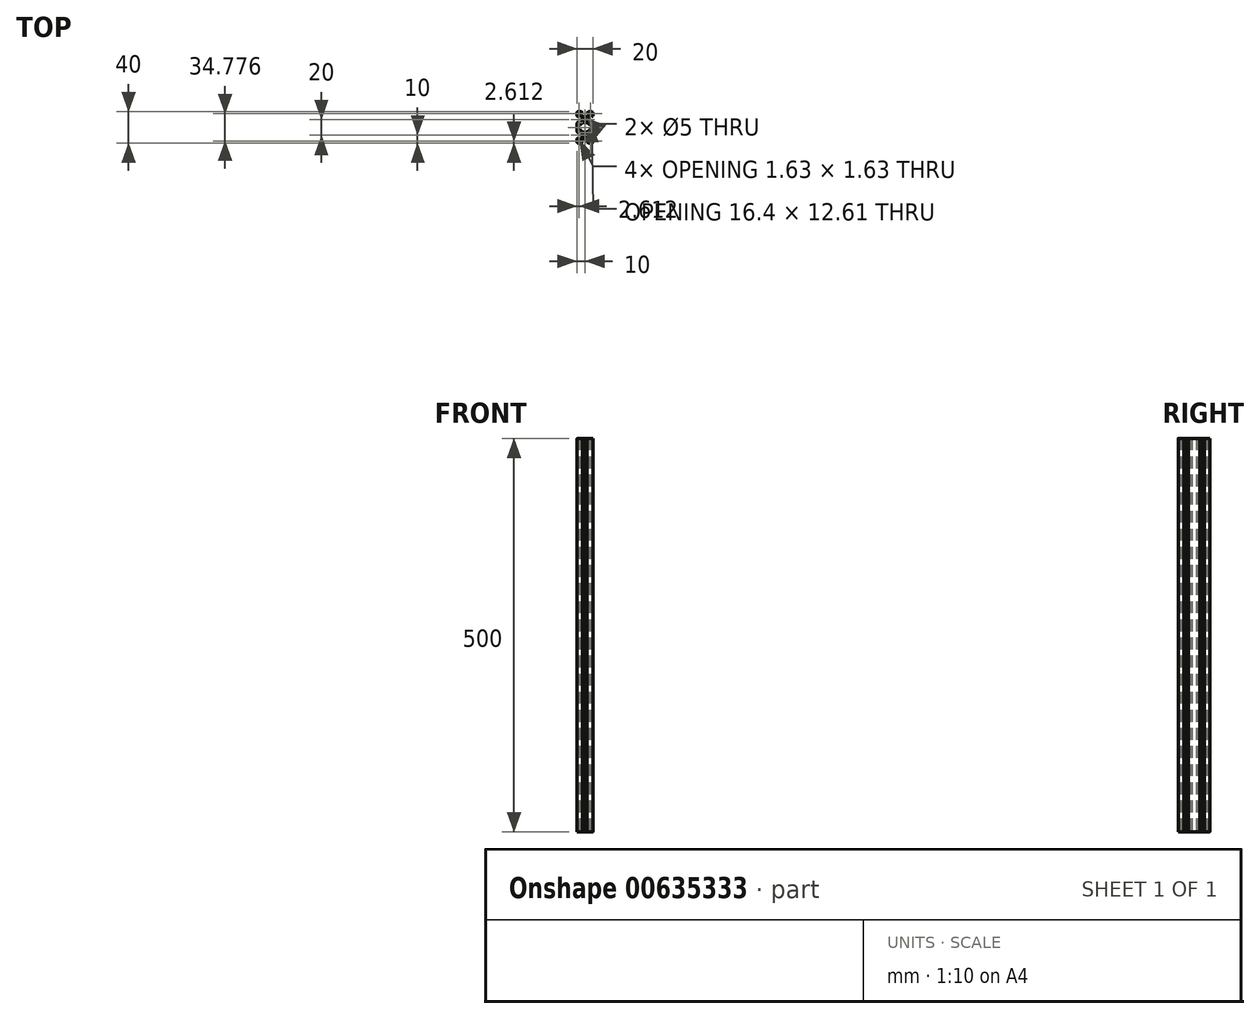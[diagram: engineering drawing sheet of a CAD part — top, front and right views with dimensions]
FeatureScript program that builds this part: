
annotation { "Feature Type Name" : "Feature", "Feature Type Description" : "" }
export const myFeature = defineFeature(function(context is Context, id is Id, definition is map)
    precondition{}
    {
        {
            var Q0;
            Q0=qCreatedBy(makeId("Top.planeOp"),FACE);
            var sketch = newSketch(context, id + "F0", { "sketchPlane" : qUnion([Q0])});
            skLineSegment(sketch, "E0.4", {"start": v(-2.85, 13.9) * mm, "end": v(-0.2, 13.9) * mm});
            skArc(sketch, "E0.48", {"start": v(-4.4, 19.82) * mm, "mid": v(-4.6, 19.95) * mm, "end": v(-4.82, 20) * mm});
            skLineSegment(sketch, "E0.49", {"start": v(-5.5, 16.55) * mm, "end": v(-2.85, 13.9) * mm});
            skLineSegment(sketch, "E0.72", {"start": v(-6.57, 17.66) * mm, "end": v(-6.57, 18.2) * mm});
            skLineSegment(sketch, "E0.103", {"start": v(-2.89, 18.2) * mm, "end": v(-5.5, 18.2) * mm});
            skArc(sketch, "E0.110", {"start": v(-8.5, 20) * mm, "mid": v(-9.07, 19.89) * mm, "end": v(-9.56, 19.56) * mm});
            skLineSegment(sketch, "E0.124", {"start": v(-5.5, 18.2) * mm, "end": v(-5.5, 16.55) * mm});
            skLineSegment(sketch, "E0.201", {"start": v(-4.4, 19.82) * mm, "end": v(-2.89, 18.3) * mm});
            skCircle(sketch, "E0.222", {"center": v(0, 10) * mm, "radius": 2.5 * mm});
            skLineSegment(sketch, "E0.289", {"start": v(-8.5, 20) * mm, "end": v(-4.82, 20) * mm});
            skLineSegment(sketch, "E0.340", {"start": v(-2.89, 18.3) * mm, "end": v(-2.89, 18.2) * mm});
            skLineSegment(sketch, "E0.361", {"start": v(-6.57, 18.2) * mm, "end": v(-8.2, 18.2) * mm});
            skLineSegment(sketch, "E0.440", {"start": v(-0.2, 13.9) * mm, "end": v(0, 13.7) * mm});
            skLineSegment(sketch, "E1", {"start": v(0, 10) * mm, "end": v(-14.3, 24.3) * mm, "construction": true});
            skLineSegment(sketch, "E2", {"start": v(-6.57, 17.66) * mm, "end": v(-7.12, 17.12) * mm});
            skLineSegment(sketch, "E3.MirrorCS", {"start": v(-8.3, 12.89) * mm, "end": v(-8.2, 12.89) * mm});
            skLineSegment(sketch, "E4.MirrorCS", {"start": v(-3.9, 10.2) * mm, "end": v(-3.7, 10) * mm});
            skLineSegment(sketch, "E5.MirrorCS", {"start": v(-10, 18.5) * mm, "end": v(-10, 14.82) * mm});
            skLineSegment(sketch, "E6.MirrorCS", {"start": v(-9.82, 14.4) * mm, "end": v(-8.3, 12.89) * mm});
            skLineSegment(sketch, "E7.MirrorCS", {"start": v(-3.9, 12.85) * mm, "end": v(-3.9, 10.2) * mm});
            skLineSegment(sketch, "E8.MirrorCS", {"start": v(-8.2, 15.5) * mm, "end": v(-6.55, 15.5) * mm});
            skLineSegment(sketch, "E9.MirrorCS", {"start": v(-8.2, 16.57) * mm, "end": v(-8.2, 18.2) * mm});
            skLineSegment(sketch, "E10.MirrorCS", {"start": v(-7.66, 16.57) * mm, "end": v(-8.2, 16.57) * mm});
            skArc(sketch, "E11.MirrorCS", {"start": v(-9.82, 14.4) * mm, "mid": v(-9.95, 14.6) * mm, "end": v(-10, 14.82) * mm});
            skArc(sketch, "E12.MirrorCS", {"start": v(-10, 18.5) * mm, "mid": v(-9.89, 19.07) * mm, "end": v(-9.56, 19.56) * mm});
            skLineSegment(sketch, "E13.MirrorCS", {"start": v(-7.66, 16.57) * mm, "end": v(-7.12, 17.12) * mm});
            skLineSegment(sketch, "E14.MirrorCS", {"start": v(-8.2, 12.89) * mm, "end": v(-8.2, 15.5) * mm});
            skLineSegment(sketch, "E15.MirrorCS", {"start": v(-6.55, 15.5) * mm, "end": v(-3.9, 12.85) * mm});
            skLineSegment(sketch, "E16", {"start": v(0, 10) * mm, "end": v(0, 23.95) * mm, "construction": true});
            skLineSegment(sketch, "E17.MirrorCS", {"start": v(6.57, 17.66) * mm, "end": v(6.57, 18.2) * mm});
            skLineSegment(sketch, "E18.MirrorCS", {"start": v(2.89, 18.3) * mm, "end": v(2.89, 18.2) * mm});
            skLineSegment(sketch, "E19.MirrorCS", {"start": v(7.66, 16.57) * mm, "end": v(7.12, 17.12) * mm});
            skArc(sketch, "E20.MirrorCS", {"start": v(9.82, 14.4) * mm, "mid": v(9.95, 14.6) * mm, "end": v(10, 14.82) * mm});
            skLineSegment(sketch, "E21.MirrorCS", {"start": v(0.2, 13.9) * mm, "end": v(0, 13.7) * mm});
            skLineSegment(sketch, "E22.MirrorCS", {"start": v(7.66, 16.57) * mm, "end": v(8.2, 16.57) * mm});
            skLineSegment(sketch, "E23.MirrorCS", {"start": v(6.57, 17.66) * mm, "end": v(7.12, 17.12) * mm});
            skArc(sketch, "E24.MirrorCS", {"start": v(4.4, 19.82) * mm, "mid": v(4.6, 19.95) * mm, "end": v(4.82, 20) * mm});
            skLineSegment(sketch, "E25.MirrorCS", {"start": v(3.9, 10.2) * mm, "end": v(3.7, 10) * mm});
            skLineSegment(sketch, "E26.MirrorCS", {"start": v(8.3, 12.89) * mm, "end": v(8.2, 12.89) * mm});
            skLineSegment(sketch, "E27.MirrorCS", {"start": v(5.5, 18.2) * mm, "end": v(5.5, 16.55) * mm});
            skLineSegment(sketch, "E28.MirrorCS", {"start": v(9.82, 14.4) * mm, "end": v(8.3, 12.89) * mm});
            skLineSegment(sketch, "E29.MirrorCS", {"start": v(8.2, 16.57) * mm, "end": v(8.2, 18.2) * mm});
            skLineSegment(sketch, "E30.MirrorCS", {"start": v(5.5, 16.55) * mm, "end": v(2.85, 13.9) * mm});
            skLineSegment(sketch, "E31.MirrorCS", {"start": v(2.89, 18.2) * mm, "end": v(5.5, 18.2) * mm});
            skLineSegment(sketch, "E32.MirrorCS", {"start": v(4.4, 19.82) * mm, "end": v(2.89, 18.3) * mm});
            skLineSegment(sketch, "E33.MirrorCS", {"start": v(3.9, 12.85) * mm, "end": v(3.9, 10.2) * mm});
            skLineSegment(sketch, "E34.MirrorCS", {"start": v(8.2, 12.89) * mm, "end": v(8.2, 15.5) * mm});
            skLineSegment(sketch, "E35.MirrorCS", {"start": v(2.85, 13.9) * mm, "end": v(0.2, 13.9) * mm});
            skLineSegment(sketch, "E36.MirrorCS", {"start": v(8.5, 20) * mm, "end": v(4.82, 20) * mm});
            skLineSegment(sketch, "E37.MirrorCS", {"start": v(10, 18.5) * mm, "end": v(10, 14.82) * mm});
            skLineSegment(sketch, "E38.MirrorCS", {"start": v(6.57, 18.2) * mm, "end": v(8.2, 18.2) * mm});
            skArc(sketch, "E39.MirrorCS", {"start": v(10, 18.5) * mm, "mid": v(9.89, 19.07) * mm, "end": v(9.56, 19.56) * mm});
            skLineSegment(sketch, "E40.MirrorCS", {"start": v(6.55, 15.5) * mm, "end": v(3.9, 12.85) * mm});
            skArc(sketch, "E41.MirrorCS", {"start": v(8.5, 20) * mm, "mid": v(9.07, 19.89) * mm, "end": v(9.56, 19.56) * mm});
            skLineSegment(sketch, "E42.MirrorCS", {"start": v(8.2, 15.5) * mm, "end": v(6.55, 15.5) * mm});
            skLineSegment(sketch, "E43", {"start": v(0, 10) * mm, "end": v(-15.63, 10) * mm, "construction": true});
            skLineSegment(sketch, "E44.MirrorCS", {"start": v(2.85, 6.1) * mm, "end": v(0.2, 6.1) * mm});
            skLineSegment(sketch, "E45.MirrorCS", {"start": v(6.55, 4.5) * mm, "end": v(3.9, 7.15) * mm});
            skLineSegment(sketch, "E46.MirrorCS", {"start": v(3.9, 7.15) * mm, "end": v(3.9, 9.8) * mm});
            skLineSegment(sketch, "E47.MirrorCS", {"start": v(3.9, 9.8) * mm, "end": v(3.7, 10) * mm});
            skLineSegment(sketch, "E48.MirrorCS", {"start": v(8.2, 4.5) * mm, "end": v(6.55, 4.5) * mm});
            skLineSegment(sketch, "E49.MirrorCS", {"start": v(8.2, 7.11) * mm, "end": v(8.2, 4.5) * mm});
            skLineSegment(sketch, "E50.MirrorCS", {"start": v(9.82, 5.6) * mm, "end": v(8.3, 7.11) * mm});
            skArc(sketch, "E51.MirrorCS", {"start": v(9.82, 5.6) * mm, "mid": v(9.95, 5.4) * mm, "end": v(10, 5.18) * mm});
            skLineSegment(sketch, "E52", {"start": v(10, 5.18) * mm, "end": v(10, 0) * mm});
            skLineSegment(sketch, "E53", {"start": v(8.2, 0) * mm, "end": v(8.2, 2.7) * mm});
            skLineSegment(sketch, "E54", {"start": v(8.2, 2.7) * mm, "end": v(6.24, 2.7) * mm});
            skLineSegment(sketch, "E55", {"start": v(6.24, 2.7) * mm, "end": v(2.85, 6.1) * mm});
            skLineSegment(sketch, "E56.MirrorCS", {"start": v(0.2, 6.1) * mm, "end": v(0, 6.3) * mm});
            skLineSegment(sketch, "E57.MirrorCS", {"start": v(8.3, 7.11) * mm, "end": v(8.2, 7.11) * mm});
            skLineSegment(sketch, "E58.MirrorCS", {"start": v(-0.2, 6.1) * mm, "end": v(0, 6.3) * mm});
            skLineSegment(sketch, "E59.MirrorCS", {"start": v(-3.9, 9.8) * mm, "end": v(-3.7, 10) * mm});
            skLineSegment(sketch, "E60.MirrorCS", {"start": v(-3.9, 7.15) * mm, "end": v(-3.9, 9.8) * mm});
            skLineSegment(sketch, "E61.MirrorCS", {"start": v(-2.85, 6.1) * mm, "end": v(-0.2, 6.1) * mm});
            skLineSegment(sketch, "E62.MirrorCS", {"start": v(-6.24, 2.7) * mm, "end": v(-2.85, 6.1) * mm});
            skLineSegment(sketch, "E63.MirrorCS", {"start": v(-6.55, 4.5) * mm, "end": v(-3.9, 7.15) * mm});
            skLineSegment(sketch, "E64.MirrorCS", {"start": v(-8.2, 4.5) * mm, "end": v(-6.55, 4.5) * mm});
            skLineSegment(sketch, "E65.MirrorCS", {"start": v(-8.2, 2.7) * mm, "end": v(-6.24, 2.7) * mm});
            skLineSegment(sketch, "E66.MirrorCS", {"start": v(-8.2, 0) * mm, "end": v(-8.2, 2.7) * mm});
            skLineSegment(sketch, "E67.MirrorCS", {"start": v(-8.2, 7.11) * mm, "end": v(-8.2, 4.5) * mm});
            skLineSegment(sketch, "E68.MirrorCS", {"start": v(-8.3, 7.11) * mm, "end": v(-8.2, 7.11) * mm});
            skLineSegment(sketch, "E69.MirrorCS", {"start": v(-9.82, 5.6) * mm, "end": v(-8.3, 7.11) * mm});
            skArc(sketch, "E70.MirrorCS", {"start": v(-9.82, 5.6) * mm, "mid": v(-9.95, 5.4) * mm, "end": v(-10, 5.18) * mm});
            skLineSegment(sketch, "E71.MirrorCS", {"start": v(-10, 5.18) * mm, "end": v(-10, 0) * mm});
            skLineSegment(sketch, "E72", {"start": v(-21.24, 0) * mm, "end": v(17.01, 0) * mm, "construction": true});
            skLineSegment(sketch, "E73.MirrorCS", {"start": v(-0.2, -13.9) * mm, "end": v(0, -13.7) * mm});
            skLineSegment(sketch, "E74.MirrorCS", {"start": v(-6.57, -17.66) * mm, "end": v(-7.12, -17.12) * mm});
            skLineSegment(sketch, "E75.MirrorCS", {"start": v(-2.89, -18.3) * mm, "end": v(-2.89, -18.2) * mm});
            skLineSegment(sketch, "E76.MirrorCS", {"start": v(-6.57, -17.66) * mm, "end": v(-6.57, -18.2) * mm});
            skLineSegment(sketch, "E77.MirrorCS", {"start": v(0.2, -13.9) * mm, "end": v(0, -13.7) * mm});
            skLineSegment(sketch, "E78.MirrorCS", {"start": v(-8.3, -7.11) * mm, "end": v(-8.2, -7.11) * mm});
            skLineSegment(sketch, "E79.MirrorCS", {"start": v(8.3, -7.11) * mm, "end": v(8.2, -7.11) * mm});
            skLineSegment(sketch, "E80.MirrorCS", {"start": v(-3.9, -9.8) * mm, "end": v(-3.7, -10) * mm});
            skArc(sketch, "E81.MirrorCS", {"start": v(4.4, -19.82) * mm, "mid": v(4.6, -19.95) * mm, "end": v(4.82, -20) * mm});
            skLineSegment(sketch, "E82.MirrorCS", {"start": v(0.2, -6.1) * mm, "end": v(0, -6.3) * mm});
            skArc(sketch, "E83.MirrorCS", {"start": v(-4.4, -19.82) * mm, "mid": v(-4.6, -19.95) * mm, "end": v(-4.82, -20) * mm});
            skLineSegment(sketch, "E84.MirrorCS", {"start": v(3.9, -9.8) * mm, "end": v(3.7, -10) * mm});
            skLineSegment(sketch, "E85.MirrorCS", {"start": v(7.66, -16.57) * mm, "end": v(7.12, -17.12) * mm});
            skLineSegment(sketch, "E86.MirrorCS", {"start": v(-8.3, -12.89) * mm, "end": v(-8.2, -12.89) * mm});
            skLineSegment(sketch, "E87.MirrorCS", {"start": v(2.89, -18.3) * mm, "end": v(2.89, -18.2) * mm});
            skLineSegment(sketch, "E88.MirrorCS", {"start": v(3.9, -10.2) * mm, "end": v(3.7, -10) * mm});
            skLineSegment(sketch, "E89.MirrorCS", {"start": v(-7.66, -16.57) * mm, "end": v(-7.12, -17.12) * mm});
            skLineSegment(sketch, "E90.MirrorCS", {"start": v(8.3, -12.89) * mm, "end": v(8.2, -12.89) * mm});
            skArc(sketch, "E91.MirrorCS", {"start": v(9.82, -14.4) * mm, "mid": v(9.95, -14.6) * mm, "end": v(10, -14.82) * mm});
            skArc(sketch, "E92.MirrorCS", {"start": v(-9.82, -14.4) * mm, "mid": v(-9.95, -14.6) * mm, "end": v(-10, -14.82) * mm});
            skLineSegment(sketch, "E93.MirrorCS", {"start": v(-3.9, -10.2) * mm, "end": v(-3.7, -10) * mm});
            skLineSegment(sketch, "E94.MirrorCS", {"start": v(-7.66, -16.57) * mm, "end": v(-8.2, -16.57) * mm});
            skLineSegment(sketch, "E95.MirrorCS", {"start": v(6.57, -17.66) * mm, "end": v(7.12, -17.12) * mm});
            skArc(sketch, "E96.MirrorCS", {"start": v(-9.82, -5.6) * mm, "mid": v(-9.95, -5.4) * mm, "end": v(-10, -5.18) * mm});
            skArc(sketch, "E97.MirrorCS", {"start": v(9.82, -5.6) * mm, "mid": v(9.95, -5.4) * mm, "end": v(10, -5.18) * mm});
            skLineSegment(sketch, "E98.MirrorCS", {"start": v(-0.2, -6.1) * mm, "end": v(0, -6.3) * mm});
            skLineSegment(sketch, "E99.MirrorCS", {"start": v(7.66, -16.57) * mm, "end": v(8.2, -16.57) * mm});
            skLineSegment(sketch, "E100.MirrorCS", {"start": v(6.57, -17.66) * mm, "end": v(6.57, -18.2) * mm});
            skLineSegment(sketch, "E101.MirrorCS", {"start": v(-5.5, -18.2) * mm, "end": v(-5.5, -16.55) * mm});
            skArc(sketch, "E102.MirrorCS", {"start": v(-10, -18.5) * mm, "mid": v(-9.89, -19.07) * mm, "end": v(-9.56, -19.56) * mm});
            skLineSegment(sketch, "E103.MirrorCS", {"start": v(3.9, -7.15) * mm, "end": v(3.9, -9.8) * mm});
            skArc(sketch, "E104.MirrorCS", {"start": v(8.5, -20) * mm, "mid": v(9.07, -19.89) * mm, "end": v(9.56, -19.56) * mm});
            skArc(sketch, "E105.MirrorCS", {"start": v(10, -18.5) * mm, "mid": v(9.89, -19.07) * mm, "end": v(9.56, -19.56) * mm});
            skLineSegment(sketch, "E106.MirrorCS", {"start": v(8.2, -15.5) * mm, "end": v(6.55, -15.5) * mm});
            skLineSegment(sketch, "E107.MirrorCS", {"start": v(6.57, -18.2) * mm, "end": v(8.2, -18.2) * mm});
            skLineSegment(sketch, "E108.MirrorCS", {"start": v(-8.2, -2.7) * mm, "end": v(-6.24, -2.7) * mm});
            skLineSegment(sketch, "E109.MirrorCS", {"start": v(-2.85, -6.1) * mm, "end": v(-0.2, -6.1) * mm});
            skLineSegment(sketch, "E110.MirrorCS", {"start": v(8.2, -2.7) * mm, "end": v(6.24, -2.7) * mm});
            skLineSegment(sketch, "E111.MirrorCS", {"start": v(-6.55, -15.5) * mm, "end": v(-3.9, -12.85) * mm});
            skLineSegment(sketch, "E112.MirrorCS", {"start": v(6.24, -2.7) * mm, "end": v(2.85, -6.1) * mm});
            skLineSegment(sketch, "E113.MirrorCS", {"start": v(-8.2, -16.57) * mm, "end": v(-8.2, -18.2) * mm});
            skLineSegment(sketch, "E114.MirrorCS", {"start": v(8.2, -7.11) * mm, "end": v(8.2, -4.5) * mm});
            skLineSegment(sketch, "E115.MirrorCS", {"start": v(8.2, 0) * mm, "end": v(8.2, -2.7) * mm});
            skLineSegment(sketch, "E116.MirrorCS", {"start": v(-8.2, -4.5) * mm, "end": v(-6.55, -4.5) * mm});
            skLineSegment(sketch, "E117.MirrorCS", {"start": v(6.55, -15.5) * mm, "end": v(3.9, -12.85) * mm});
            skLineSegment(sketch, "E118.MirrorCS", {"start": v(4.4, -19.82) * mm, "end": v(2.89, -18.3) * mm});
            skLineSegment(sketch, "E119.MirrorCS", {"start": v(3.9, -12.85) * mm, "end": v(3.9, -10.2) * mm});
            skLineSegment(sketch, "E120.MirrorCS", {"start": v(9.82, -5.6) * mm, "end": v(8.3, -7.11) * mm});
            skLineSegment(sketch, "E121.MirrorCS", {"start": v(10, -18.5) * mm, "end": v(10, -14.82) * mm});
            skLineSegment(sketch, "E122.MirrorCS", {"start": v(8.2, -12.89) * mm, "end": v(8.2, -15.5) * mm});
            skLineSegment(sketch, "E123.MirrorCS", {"start": v(9.82, -14.4) * mm, "end": v(8.3, -12.89) * mm});
            skLineSegment(sketch, "E124.MirrorCS", {"start": v(-8.2, -12.89) * mm, "end": v(-8.2, -15.5) * mm});
            skArc(sketch, "E125.MirrorCS", {"start": v(-8.5, -20) * mm, "mid": v(-9.07, -19.89) * mm, "end": v(-9.56, -19.56) * mm});
            skLineSegment(sketch, "E126.MirrorCS", {"start": v(8.2, -4.5) * mm, "end": v(6.55, -4.5) * mm});
            skLineSegment(sketch, "E127.MirrorCS", {"start": v(-6.55, -4.5) * mm, "end": v(-3.9, -7.15) * mm});
            skLineSegment(sketch, "E128.MirrorCS", {"start": v(-3.9, -12.85) * mm, "end": v(-3.9, -10.2) * mm});
            skLineSegment(sketch, "E129.MirrorCS", {"start": v(-2.85, -13.9) * mm, "end": v(-0.2, -13.9) * mm});
            skLineSegment(sketch, "E130.MirrorCS", {"start": v(0, -10) * mm, "end": v(-15.63, -10) * mm, "construction": true});
            skLineSegment(sketch, "E131.MirrorCS", {"start": v(-4.4, -19.82) * mm, "end": v(-2.89, -18.3) * mm});
            skLineSegment(sketch, "E132.MirrorCS", {"start": v(-8.2, 0) * mm, "end": v(-8.2, -2.7) * mm});
            skLineSegment(sketch, "E133.MirrorCS", {"start": v(2.89, -18.2) * mm, "end": v(5.5, -18.2) * mm});
            skLineSegment(sketch, "E134.MirrorCS", {"start": v(10, -5.18) * mm, "end": v(10, 0) * mm});
            skLineSegment(sketch, "E135.MirrorCS", {"start": v(5.5, -18.2) * mm, "end": v(5.5, -16.55) * mm});
            skLineSegment(sketch, "E136.MirrorCS", {"start": v(-10, -5.18) * mm, "end": v(-10, 0) * mm});
            skLineSegment(sketch, "E137.MirrorCS", {"start": v(-3.9, -7.15) * mm, "end": v(-3.9, -9.8) * mm});
            skLineSegment(sketch, "E138.MirrorCS", {"start": v(-10, -18.5) * mm, "end": v(-10, -14.82) * mm});
            skLineSegment(sketch, "E139.MirrorCS", {"start": v(2.85, -13.9) * mm, "end": v(0.2, -13.9) * mm});
            skLineSegment(sketch, "E140.MirrorCS", {"start": v(8.5, -20) * mm, "end": v(4.82, -20) * mm});
            skLineSegment(sketch, "E141.MirrorCS", {"start": v(-9.82, -14.4) * mm, "end": v(-8.3, -12.89) * mm});
            skLineSegment(sketch, "E142.MirrorCS", {"start": v(8.2, -16.57) * mm, "end": v(8.2, -18.2) * mm});
            skLineSegment(sketch, "E143.MirrorCS", {"start": v(-9.82, -5.6) * mm, "end": v(-8.3, -7.11) * mm});
            skCircle(sketch, "E144.MirrorC", {"center": v(0, -10) * mm, "radius": 2.5 * mm});
            skLineSegment(sketch, "E145.MirrorCS", {"start": v(-2.89, -18.2) * mm, "end": v(-5.5, -18.2) * mm});
            skLineSegment(sketch, "E146.MirrorCS", {"start": v(-6.57, -18.2) * mm, "end": v(-8.2, -18.2) * mm});
            skLineSegment(sketch, "E147.MirrorCS", {"start": v(-8.2, -15.5) * mm, "end": v(-6.55, -15.5) * mm});
            skLineSegment(sketch, "E148.MirrorCS", {"start": v(-8.5, -20) * mm, "end": v(-4.82, -20) * mm});
            skLineSegment(sketch, "E149.MirrorCS", {"start": v(-5.5, -16.55) * mm, "end": v(-2.85, -13.9) * mm});
            skLineSegment(sketch, "E150.MirrorCS", {"start": v(6.55, -4.5) * mm, "end": v(3.9, -7.15) * mm});
            skLineSegment(sketch, "E151.MirrorCS", {"start": v(5.5, -16.55) * mm, "end": v(2.85, -13.9) * mm});
            skLineSegment(sketch, "E152.MirrorCS", {"start": v(-8.2, -7.11) * mm, "end": v(-8.2, -4.5) * mm});
            skLineSegment(sketch, "E153.MirrorCS", {"start": v(2.85, -6.1) * mm, "end": v(0.2, -6.1) * mm});
            skLineSegment(sketch, "E154.MirrorCS", {"start": v(-6.24, -2.7) * mm, "end": v(-2.85, -6.1) * mm});
            skSolve(sketch);
        }
        {
            var Q0;
            Q0=makeQuery(id+"F0.imprint","IMPRINT",FACE,{"disambiguationData":[TD([[makeQuery(id+"F0.imprint","IMPRINT",EDGE,{"derivedFrom":sQuery(id+"F0.wireOp",EDGE,"E0.4")}),-1.0]])]});
            extrude(context, id + "F1", {"entities" : qUnion([Q0]), "depth" : 500 * mm, "offsetDistance" : 25 * mm});
        }
    });
